# Revit family: Shower-Shower_Arm-KOHLER-K-26318IN
name_source: partatom
category: Plumbing Fixtures
revit_build: Autodesk Revit 2017 (Build: 20160225_1515(x64)
units: mm (PartAtom-declared; Revit-internal decimal feet)

## family parameters
Cut with Voids When Loaded = No
Host = Face
OmniClass Number = 23.31.17.00
OmniClass Title = Showers
Part Type = Normal
Room Calculation Point = No
Round Connector Dimension = Use Diameter
Shared = No

## types (6) — shared parameters
ADA Compliant = No
Assembly Code = D2010700
CW Connection = Yes
Cold Water Inlet = Cold Water Inlet
Date Modified = 02/09/2020
Description = Shower Arm
Drain Included = No
Flow Rate = 0 GPM
HW Connection = Yes
Height = 3"
Hot Water Inlet = Hot Water Inlet
Length = 5 13/16"
Manufacturer = KOHLER Co.
Master Format 2014 = 22 42 23
Master Format 2014 Name = Residential Showers
Material = Brass Construction
Pressure = 0.00 psi
Tempered Water Inlet = Tempered Water Inlet
URL = https://www.kohler.co.in
Vent Connection = No
Waste Connection = No
Waste Water Outlet = Waste Water Outlet
WaterSense Certified = No
Width = 2 3/16"

## per-type parameters (varying)
| type | Default Elevation | Finish | Model | Type |
| CP-Polished Chrome | 72" | Kohler-Metal-CP-Polished_Chrome | K-26318IN-CP | 1 |
| BL-Matte Black | 0" | Kohler-Metal-BL-Matte_Black | K-26318IN-BL | 3 |
| BN-Brushed Nickel | 42" | Kohler-Metal-BN-Roman_Silver | K-26318IN-BN | 4 |
| AF-French Gold | 42" | Kohler-Metal-AF-Vibrant_French_Gold | K-26318IN-AF | 2 |
| BV-Brushed Bronze | 42" | Kohler-Metal-BV-Brushed_Bronze | K-26318IN-BV | 5 |
| RGD-Rose Gold | 42" | Kohler-Metal-RGD-Polished_Rose_Gold | K-26318IN-RGD | 6 |

## geometry (parser evidence)
native form markers: Sweep x6
no freeform markers — native parametric forms only
